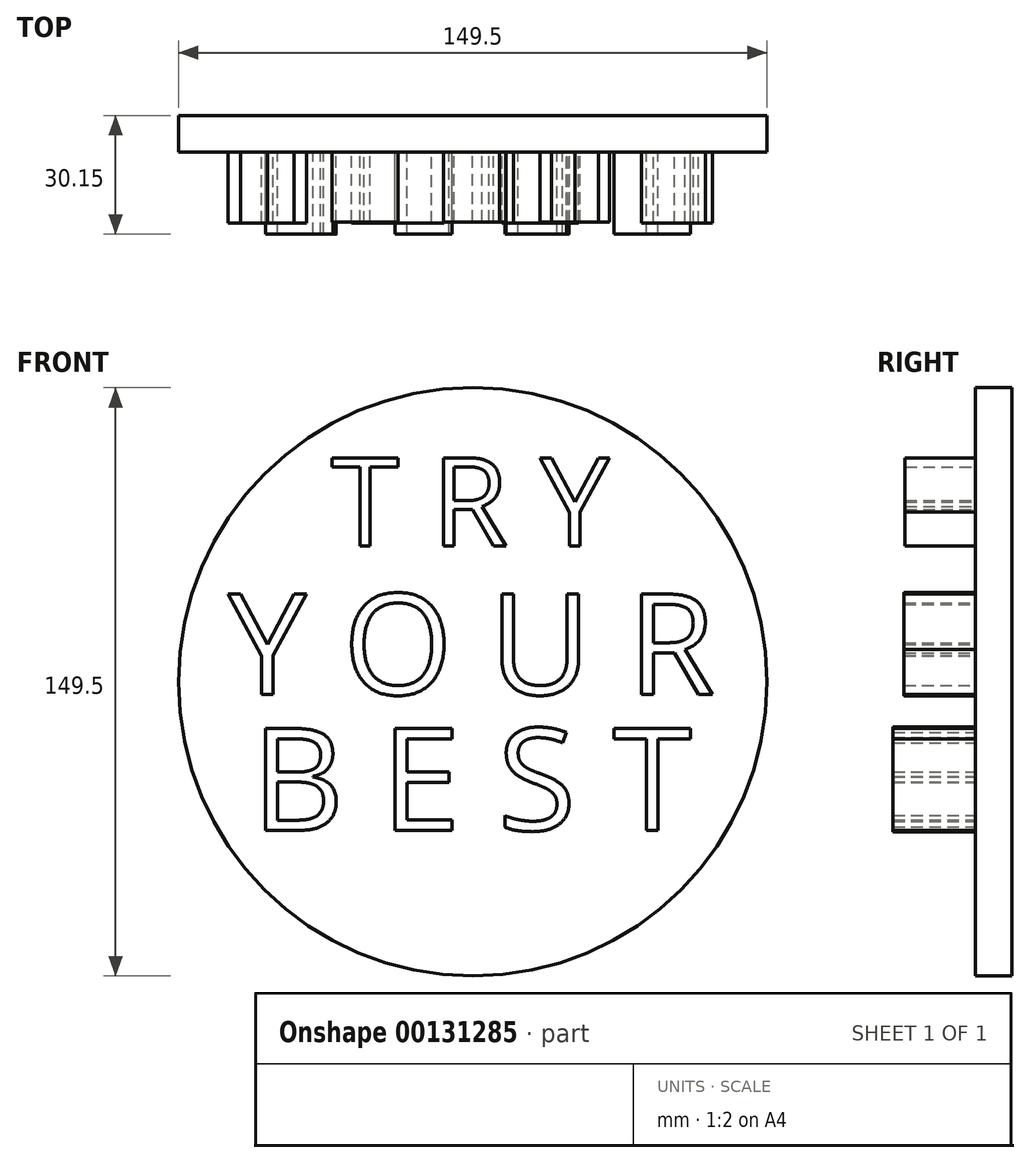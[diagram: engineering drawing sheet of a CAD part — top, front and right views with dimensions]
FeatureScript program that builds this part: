
annotation { "Feature Type Name" : "Feature", "Feature Type Description" : "" }
export const myFeature = defineFeature(function(context is Context, id is Id, definition is map)
    precondition{}
    {
        {
            var Q0;
            Q0=qCreatedBy(makeId("Front.planeOp"),FACE);
            var sketch = newSketch(context, id + "F0", { "sketchPlane" : qUnion([Q0])});
            skCircle(sketch, "E0", {"center": v(0, 0) * mm, "radius": 74.75 * mm});
            skSolve(sketch);
        }
        {
            var Q0;
            Q0=makeQuery(id+"F0.imprint","IMPRINT",FACE,{"disambiguationData":[TD([[makeQuery(id+"F0.imprint","IMPRINT",EDGE,{"derivedFrom":sQuery(id+"F0.wireOp",EDGE,"E0")}),1.0]])]});
            extrude(context, id + "F1", {"entities" : qUnion([Q0]), "oppositeDirection" : true, "depth" : 9.25 * mm});
        }
        {
            var Q0;
            Q0=makeQuery(id+"F1.opExtrude","CAP_FACE",FACE,{"disambiguationData":[OSD([sQuery(id+"F0.wireOp",EDGE,"E0")])],"isStart":false});
            extrude(context, id + "F2", {"entities" : qUnion([Q0]), "operationType" : NewBodyOperationType.ADD, "oppositeDirection" : true, "depth" : 8.9 * mm});
        }
        {
            var Q0;
            Q0=makeQuery(id+"F1.opExtrude","CAP_FACE",FACE,{"disambiguationData":[OSD([sQuery(id+"F0.wireOp",EDGE,"E0")])],"isStart":true});
            var sketch = newSketch(context, id + "F3", { "sketchPlane" : qUnion([Q0])});
            skText(sketch, "E1", { "text": "T R Y", "fontName": "OpenSans-Regular.ttf"});
            const initialGuessF3  = {"E1": [-0.03606, 0.03448, 1, 0, 0.02264]};
            skSetInitialGuess(sketch, initialGuessF3);
            skSolve(sketch);
        }
        {
            var Q0;
            Q0=makeQuery(id+"F3.imprint","IMPRINT",FACE,{"disambiguationData":[TD([[makeQuery(id+"F3.imprint","IMPRINT",EDGE,{"derivedFrom":sQuery(id+"F3.wireOp",EDGE,"E1.sketch_text.stroke-0")}),1.0]])]});
            var sketch = newSketch(context, id + "F4", { "sketchPlane" : qUnion([Q0])});
            skText(sketch, "E2", { "text": "Y O U R", "fontName": "OpenSans-Regular.ttf"});
            const initialGuessF4  = {"E2": [-0.06219, -0.0032, 1, 0, 0.0257]};
            skSetInitialGuess(sketch, initialGuessF4);
            skSolve(sketch);
        }
        {
            var Q0;
            Q0=makeQuery(id+"F3.imprint","IMPRINT",FACE,{"disambiguationData":[TD([[makeQuery(id+"F3.imprint","IMPRINT",EDGE,{"derivedFrom":sQuery(id+"F3.wireOp",EDGE,"E1.sketch_text.stroke-0")}),1.0]])]});
            var sketch = newSketch(context, id + "F5", { "sketchPlane" : qUnion([Q0])});
            skText(sketch, "E3", { "text": "B E S T", "fontName": "OpenSans-Regular.ttf"});
            const initialGuessF5  = {"E3": [-0.05616, -0.03771, 1, 0, 0.02608]};
            skSetInitialGuess(sketch, initialGuessF5);
            skSolve(sketch);
        }
        {
            var Q0;
            Q0 = qSketchRegion(id + "F3", true);
            extrude(context, id + "F6", {"entities" : qUnion([Q0]), "operationType" : NewBodyOperationType.ADD, "depth" : 17.82 * mm});
        }
        {
            var Q0;
            Q0 = qSketchRegion(id + "F4", true);
            extrude(context, id + "F7", {"entities" : qUnion([Q0]), "operationType" : NewBodyOperationType.ADD, "depth" : 18.1 * mm});
        }
        {
            var Q0;
            Q0 = qSketchRegion(id + "F5", true);
            extrude(context, id + "F8", {"entities" : qUnion([Q0]), "operationType" : NewBodyOperationType.ADD, "depth" : 20.9 * mm});
        }
    });
